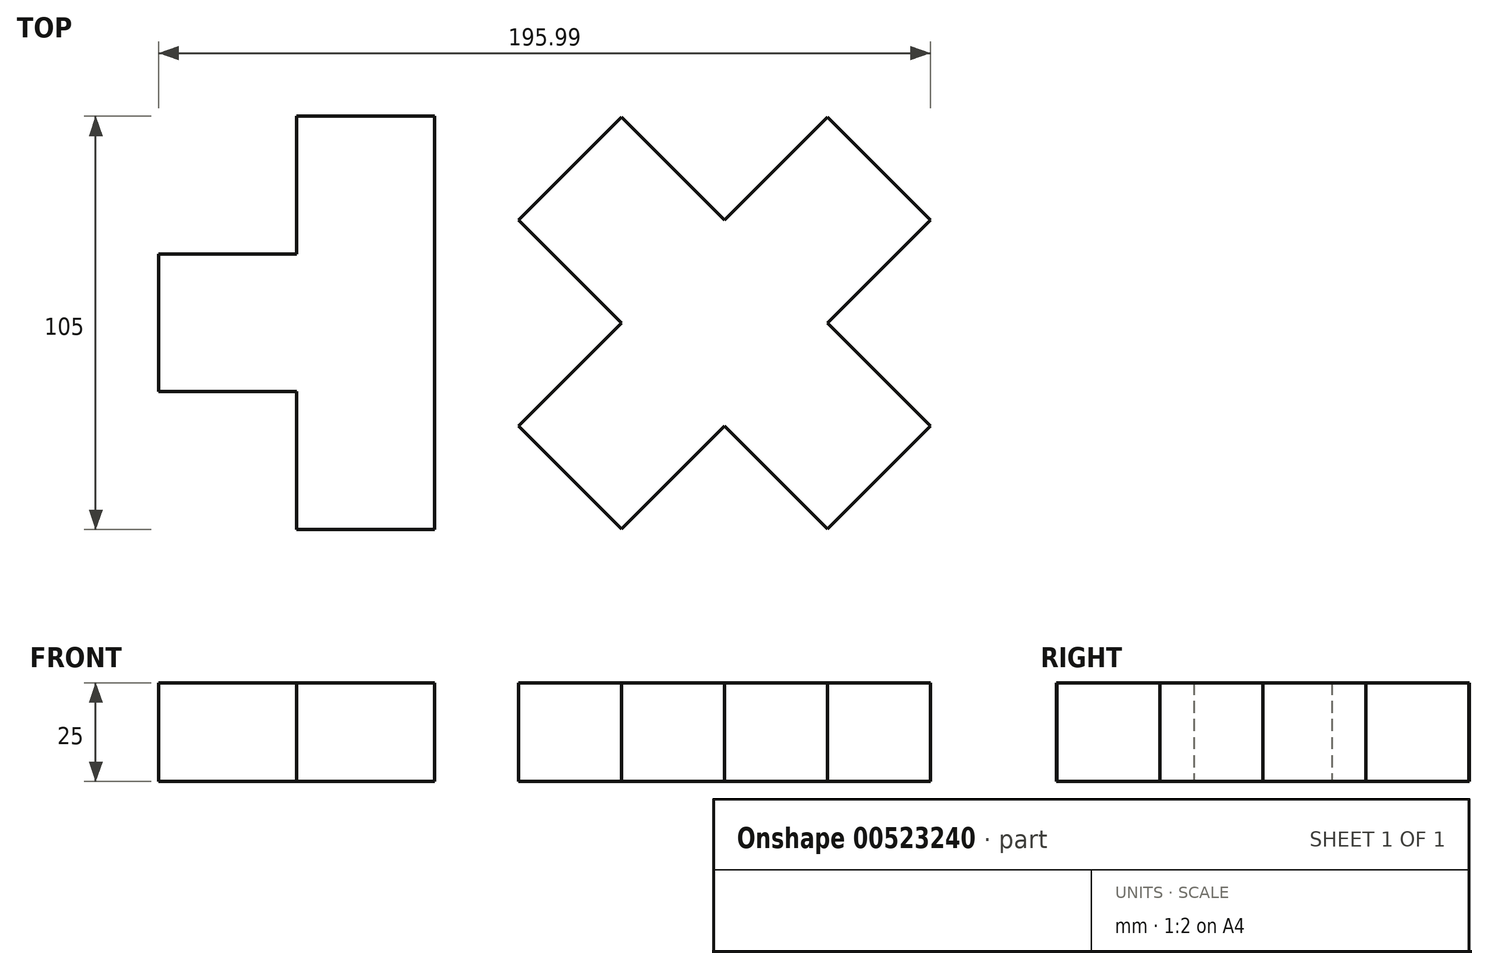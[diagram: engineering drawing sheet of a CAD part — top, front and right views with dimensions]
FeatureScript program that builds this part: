
annotation { "Feature Type Name" : "Feature", "Feature Type Description" : "" }
export const myFeature = defineFeature(function(context is Context, id is Id, definition is map)
    precondition{}
    {
        {
            var Q0;
            Q0=qCreatedBy(makeId("Top.planeOp"),FACE);
            var sketch = newSketch(context, id + "F0", { "sketchPlane" : qUnion([Q0])});
            skLineSegment(sketch, "E0", {"start": v(-5.14, 42.66) * mm, "end": v(29.86, 42.66) * mm});
            skLineSegment(sketch, "E1", {"start": v(29.86, 42.66) * mm, "end": v(29.86, 7.66) * mm});
            skLineSegment(sketch, "E2", {"start": v(29.86, 7.66) * mm, "end": v(64.86, 7.66) * mm});
            skLineSegment(sketch, "E3", {"start": v(64.86, 7.66) * mm, "end": v(64.86, -27.34) * mm});
            skLineSegment(sketch, "E4", {"start": v(64.86, -27.34) * mm, "end": v(29.86, -27.34) * mm});
            skLineSegment(sketch, "E5", {"start": v(29.86, -27.34) * mm, "end": v(29.86, -62.34) * mm});
            skLineSegment(sketch, "E6", {"start": v(29.86, -62.34) * mm, "end": v(-5.14, -62.34) * mm});
            skLineSegment(sketch, "E7", {"start": v(-5.14, -62.34) * mm, "end": v(-5.14, -27.34) * mm});
            skLineSegment(sketch, "E8", {"start": v(-5.14, -27.34) * mm, "end": v(-40.14, -27.34) * mm});
            skLineSegment(sketch, "E9", {"start": v(-40.14, -27.34) * mm, "end": v(-40.14, 7.66) * mm});
            skLineSegment(sketch, "E10", {"start": v(-40.14, 7.66) * mm, "end": v(-5.14, 7.66) * mm});
            skLineSegment(sketch, "E11", {"start": v(-5.14, 7.66) * mm, "end": v(-5.14, 42.66) * mm});
            skLineSegment(sketch, "E12", {"start": v(51.2, 16.32) * mm, "end": v(77.36, 42.49) * mm});
            skLineSegment(sketch, "E13", {"start": v(77.36, 42.49) * mm, "end": v(103.52, 16.32) * mm});
            skLineSegment(sketch, "E14", {"start": v(51.2, -36) * mm, "end": v(77.36, -62.16) * mm});
            skLineSegment(sketch, "E15", {"start": v(77.36, -62.16) * mm, "end": v(103.52, -36) * mm});
            skLineSegment(sketch, "E16", {"start": v(103.52, -36) * mm, "end": v(129.69, -62.16) * mm});
            skLineSegment(sketch, "E17", {"start": v(129.69, -62.16) * mm, "end": v(155.85, -36) * mm});
            skLineSegment(sketch, "E18", {"start": v(155.85, -36) * mm, "end": v(129.69, -9.84) * mm});
            skLineSegment(sketch, "E19", {"start": v(129.69, -9.84) * mm, "end": v(155.85, 16.32) * mm});
            skLineSegment(sketch, "E20", {"start": v(155.85, 16.32) * mm, "end": v(129.69, 42.49) * mm});
            skLineSegment(sketch, "E21", {"start": v(129.69, 42.49) * mm, "end": v(103.52, 16.32) * mm});
            skLineSegment(sketch, "E22", {"start": v(51.2, -36) * mm, "end": v(77.36, -9.84) * mm});
            skLineSegment(sketch, "E23", {"start": v(77.36, -9.84) * mm, "end": v(51.2, 16.32) * mm});
            skLineSegment(sketch, "E24", {"start": v(29.86, 7.66) * mm, "end": v(29.86, -27.34) * mm});
            skLineSegment(sketch, "E25", {"start": v(29.86, -9.84) * mm, "end": v(155.85, -9.84) * mm});
            skLineSegment(sketch, "E26", {"start": v(103.52, 16.32) * mm, "end": v(103.52, -36) * mm});
            skLineSegment(sketch, "E27", {"start": v(77.36, -9.84) * mm, "end": v(129.69, -9.84) * mm});
            skPoint(sketch, "E28", {"position": v(103.52, -9.84) * mm});
            skLineSegment(sketch, "E29", {"start": v(155.85, 16.32) * mm, "end": v(155.85, -36) * mm});
            skPoint(sketch, "E30", {"position": v(59.86, 7.66) * mm});
            skPoint(sketch, "E31", {"position": v(64.86, 2.66) * mm});
            skLineSegment(sketch, "E32", {"start": v(59.86, 7.66) * mm, "end": v(64.86, 2.66) * mm});
            skPoint(sketch, "E33", {"position": v(59.86, -27.34) * mm});
            skPoint(sketch, "E34", {"position": v(64.86, -22.34) * mm});
            skLineSegment(sketch, "E35", {"start": v(59.86, -27.34) * mm, "end": v(64.86, -22.34) * mm});
            skSolve(sketch);
        }
        {
            var Q0;
            Q0=makeQuery(id+"F0.imprint","IMPRINT",FACE,{"disambiguationData":[TD([[makeQuery(id+"F0.imprint","IMPRINT",EDGE,{"derivedFrom":sQuery(id+"F0.wireOp",EDGE,"E0")}),-1.0]])]});
            var Q1;
            {var subQ0=sQuery(id+"F0.wireOp",EDGE,"E2");Q1=makeQuery(id+"F0.imprint","IMPRINT",FACE,{"disambiguationData":[TD([[makeQuery(id+"F0.imprint","IMPRINT",EDGE,{"derivedFrom":subQ0}),-1.0]])]});}
            var Q2;
            {var subQ0=sQuery(id+"F0.wireOp",EDGE,"E4");Q2=makeQuery(id+"F0.imprint","IMPRINT",FACE,{"disambiguationData":[TD([[makeQuery(id+"F0.imprint","IMPRINT",EDGE,{"derivedFrom":subQ0}),-1.0]])]});}
            var Q3;
            {var subQ2=sQuery(id+"F0.wireOp",EDGE,"E12");Q3=makeQuery(id+"F0.imprint","IMPRINT",FACE,{"disambiguationData":[TD([[makeQuery(id+"F0.imprint","IMPRINT",EDGE,{"derivedFrom":subQ2}),-1.0]])]});}
            var Q4;
            {var subQ4=sQuery(id+"F0.wireOp",EDGE,"E14");Q4=makeQuery(id+"F0.imprint","IMPRINT",FACE,{"disambiguationData":[TD([[makeQuery(id+"F0.imprint","IMPRINT",EDGE,{"derivedFrom":subQ4}),1.0]])]});}
            var Q5;
            {var subQ4=sQuery(id+"F0.wireOp",EDGE,"E19");Q5=makeQuery(id+"F0.imprint","IMPRINT",FACE,{"disambiguationData":[TD([[makeQuery(id+"F0.imprint","IMPRINT",EDGE,{"derivedFrom":subQ4}),1.0]])]});}
            var Q6;
            {var subQ2=sQuery(id+"F0.wireOp",EDGE,"E16");Q6=makeQuery(id+"F0.imprint","IMPRINT",FACE,{"disambiguationData":[TD([[makeQuery(id+"F0.imprint","IMPRINT",EDGE,{"derivedFrom":subQ2}),1.0]])]});}
            var Q7;
            {var subQ7=sQuery(id+"F0.wireOp",EDGE,"E32");Q7=makeQuery(id+"F0.imprint","IMPRINT",FACE,{"disambiguationData":[TD([[makeQuery(id+"F0.imprint","IMPRINT",EDGE,{"derivedFrom":subQ7}),-1.0]])]});}
            var Q8;
            {var subQ7=sQuery(id+"F0.wireOp",EDGE,"E35");Q8=makeQuery(id+"F0.imprint","IMPRINT",FACE,{"disambiguationData":[TD([[makeQuery(id+"F0.imprint","IMPRINT",EDGE,{"derivedFrom":subQ7}),1.0]])]});}
            extrude(context, id + "F1", {"entities" : qUnion([Q0, Q1, Q2, Q3, Q4, Q5, Q6, Q7, Q8]), "depth" : 25 * mm, "offsetDistance" : 25 * mm});
        }
    });
